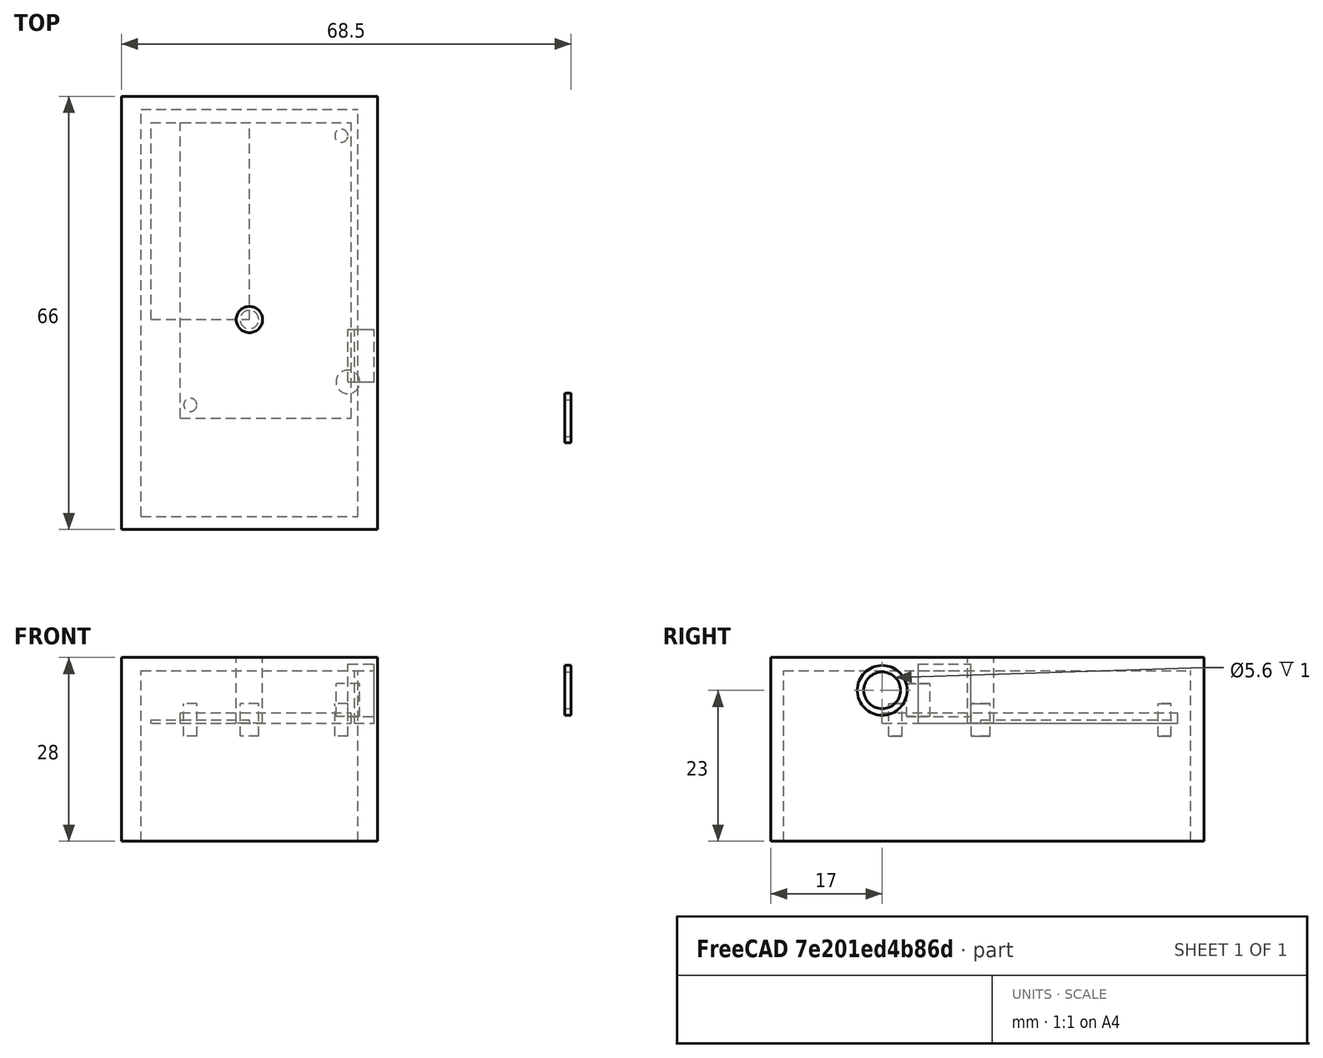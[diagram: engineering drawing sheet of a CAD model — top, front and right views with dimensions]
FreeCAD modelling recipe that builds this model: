
FCSTD DOCUMENT  (FreeCAD 0.15R4671 (Git))
Label: Sense_Beam_Rx_V3
License: All rights reserved
LicenseURL: http://en.wikipedia.org/wiki/All_rights_reserved
objects: Mesh::Feature×29, Part::Cylinder×7, Part::Box×6, Part::Cut×2
note: 15 computed .brp shape members not serialized (recipe doc carries the construction recipe); baked Part::Feature solids carry a one-line shape summary decoded from their .brp

FEATURE [Mesh::Feature] AA_Holder
  Placement = pos=(15,30,0) rot=(1,0,0;1.5708rad)
FEATURE [Mesh::Feature] APBD3224SURKCGKC_F01  label="APBD3224SURKCGKC-F01"
  Placement = pos=(16,92,-0.4) rot=(1,0,0;1.5708rad)
FEATURE [Mesh::Feature] Berg_90_2_54mm
FEATURE [Mesh::Feature] Button
  Placement = pos=(15,21,0) rot=(1,0,0;1.5708rad)
FEATURE [Mesh::Feature] Crystal_THP
  Placement = pos=(61,4,-0.4) rot=(0,-1,0;1.5708rad)
FEATURE [Mesh::Feature] KPTBD_3216SURKCGKC  label="KPTBD-3216SURKCGKC"
  Placement = pos=(15,92,-0.4) rot=(1,0,0;1.5708rad)
FEATURE [Mesh::Feature] PhotoDiode
  Placement = pos=(16,0,-0.4) rot=(1,0,0;1.5708rad)
FEATURE [Mesh::Feature] PogoProg
  Placement = pos=(23,10,0) rot=(1,0,0;1.5708rad)
FEATURE [Mesh::Feature] SFH4545
  Placement = pos=(15,28,0) rot=(1,0,0;1.5708rad)
FEATURE [Mesh::Feature] SJ2_3586X_SMT  label="SJ2-3586X-SMT"
FEATURE [Mesh::Feature] Stereo_Socket_3_5mm_PCB_Mount_SMD_Sunrom_5543  label="Stereo Socket 3.5mm PCB Mount SMD_Sunrom_5543"
  Placement = pos=(32.9,-8.5,1.6) rot=(0,0,1;1.5708rad)
FEATURE [Mesh::Feature] TSSOP20_package_STM32  label="TSSOP20 package_STM32"
  Placement = pos=(15,45,0) rot=(1,0,0;1.5708rad)
FEATURE [Mesh::Feature] TSSOP4056
  Placement = pos=(15,-39,-0.4) rot=(0,0.707107,0.707107;3.14159rad)
FEATURE [Part::Box] Box  label="PCB"
  Height = 1.6
  Length = 26
  Placement = pos=(4.5,-15,0) rot=(0,0,1;0rad)
  Width = 45
FEATURE [Part::Box] Box001  label="Body_out"
  Height = 28
  Length = 39
  Placement = pos=(-4.5,-32,-18) rot=(0,0,1;0rad)
  Width = 66
FEATURE [Part::Box] Box002  label="Reference_Cube"
  Height = 0.5
  Length = 15
  Width = 30
FEATURE [Part::Cylinder] Cylinder  label="Mt.H001"
  Angle = 360
  Height = 5
  Placement = pos=(15,0,-2) rot=(0,0,1;0rad)
  Radius = 1.4
FEATURE [Part::Cylinder] Cylinder001  label="Mt.H002"
  Angle = 360
  Height = 5
  Placement = pos=(6,-13,-2) rot=(0,0,1;0rad)
  Radius = 1
FEATURE [Part::Cylinder] Cylinder002  label="Mt.H003"
  Angle = 360
  Height = 5
  Placement = pos=(29,28,-2) rot=(0,0,1;0rad)
  Radius = 1
FEATURE [Mesh::Feature] nRF_MDBT42Q  label="nRF-MDBT42Q"
  Placement = pos=(15.5,51,0) rot=(1,0,0;1.5708rad)
FEATURE [Mesh::Feature] SOT_23_cmpts  label="SOT-23_cmpts"
  Placement = pos=(23,25,1.6) rot=(0,0,1;1.5708rad)
FEATURE [Mesh::Feature] _402_Package  label="0402_Package"
  Placement = pos=(9.5,3,1.6) rot=(0,0,1;1.5708rad)
FEATURE [Mesh::Feature] SOT_23_cmpts001  label="SOT-23_cmpts001"
  Placement = pos=(23,21,1.6) rot=(0,0,1;1.5708rad)
FEATURE [Mesh::Feature] _402_Package001  label="0402_Package001"
  Placement = pos=(11.5,3,1.6) rot=(0,0,1;1.5708rad)
FEATURE [Mesh::Feature] _402_Package002  label="0402_Package002"
  Placement = pos=(13.5,3,1.6) rot=(0,0,1;1.5708rad)
FEATURE [Mesh::Feature] _402_Package003  label="0402_Package003"
  Placement = pos=(15.5,3,1.6) rot=(0,0,1;1.5708rad)
FEATURE [Mesh::Feature] SOT_23_cmpts002  label="SOT-23_cmpts002"
  Placement = pos=(23,17,1.6) rot=(0,0,1;1.5708rad)
FEATURE [Mesh::Feature] SOT_23_cmpts003  label="SOT-23_cmpts003"
  Placement = pos=(9,20,1.6) rot=(0,0,1;1.5708rad)
FEATURE [Mesh::Feature] SOT_23_cmpts004  label="SOT-23_cmpts004"
  Placement = pos=(22,-13,1.6) rot=(0,0,1;1.5708rad)
FEATURE [Mesh::Feature] AA_Battery_Holder_PCB_Mount
  Placement = pos=(-1,-29,0) rot=(-1,0,0;1.5708rad)
FEATURE [Part::Box] Box003  label="Body_in"
  Height = 26
  Length = 33
  Placement = pos=(-1.5,-30,-18) rot=(0,0,1;0rad)
  Width = 62
FEATURE [Part::Cut] Cut  label="Body"
  Base = -> Box001
  Tool = -> Box003
FEATURE [Part::Box] Box004  label="Audio_jack001"
  Height = 8
  Length = 4
  Placement = pos=(30,-9.5,1) rot=(0,0,1;0rad)
  Width = 8
FEATURE [Part::Cylinder] Cylinder003  label="Audio_jack002"
  Angle = 360
  Height = 5
  Placement = pos=(30,-9.5,1) rot=(0,0,1;0rad)
  Radius = 1.8
FEATURE [Part::Box] Box005  label="Audio_jack003"
  Height = 8
  Length = 3
  Placement = pos=(31,-9.5,0) rot=(0,0,1;0rad)
  Width = 8
FEATURE [Part::Cylinder] Cylinder004  label="Audio_jack004"
  Angle = 360
  Height = 1
  Placement = pos=(33,-5.5,4) rot=(0,1,0;1.5708rad)
  Radius = 2.8
FEATURE [Part::Cylinder] Cylinder005  label="Audio_jack005"
  Angle = 360
  Height = 1
  Placement = pos=(33,-5.5,4) rot=(0,1,0;1.5708rad)
  Radius = 3.8
FEATURE [Part::Cut] Cut001
  Base = -> Cylinder005
  Placement = pos=(30,-9.5,1) rot=(0,0,1;0rad)
  Tool = -> Cylinder004
FEATURE [Mesh::Feature] PJ_32434_AudioJack  label="PJ-32434_AudioJack"
  Placement = pos=(31,-9,1.6) rot=(0,0,1;1.5708rad)
FEATURE [Mesh::Feature] PogoProg2
  Placement = pos=(30,5,0) rot=(0,0,1;1.5708rad)
FEATURE [Part::Cylinder] Cylinder006  label="Mt.H004"
  Angle = 360
  Height = 10
  Placement = pos=(15,0,0) rot=(0,0,1;0rad)
  Radius = 2
FEATURE [Mesh::Feature] M3_Nut
  Placement = pos=(15,0,2) rot=(0,0,1;0rad)
FEATURE [Mesh::Feature] M3x6mm_Screw
  Placement = pos=(15,0,6) rot=(1,0,0;3.14159rad)
FEATURE [Mesh::Feature] Button_TC_1101T_C_A_B  label="Button_TC-1101T-C-A-B"
  Placement = pos=(12,-8,1.6) rot=(0,0,1;0rad)
